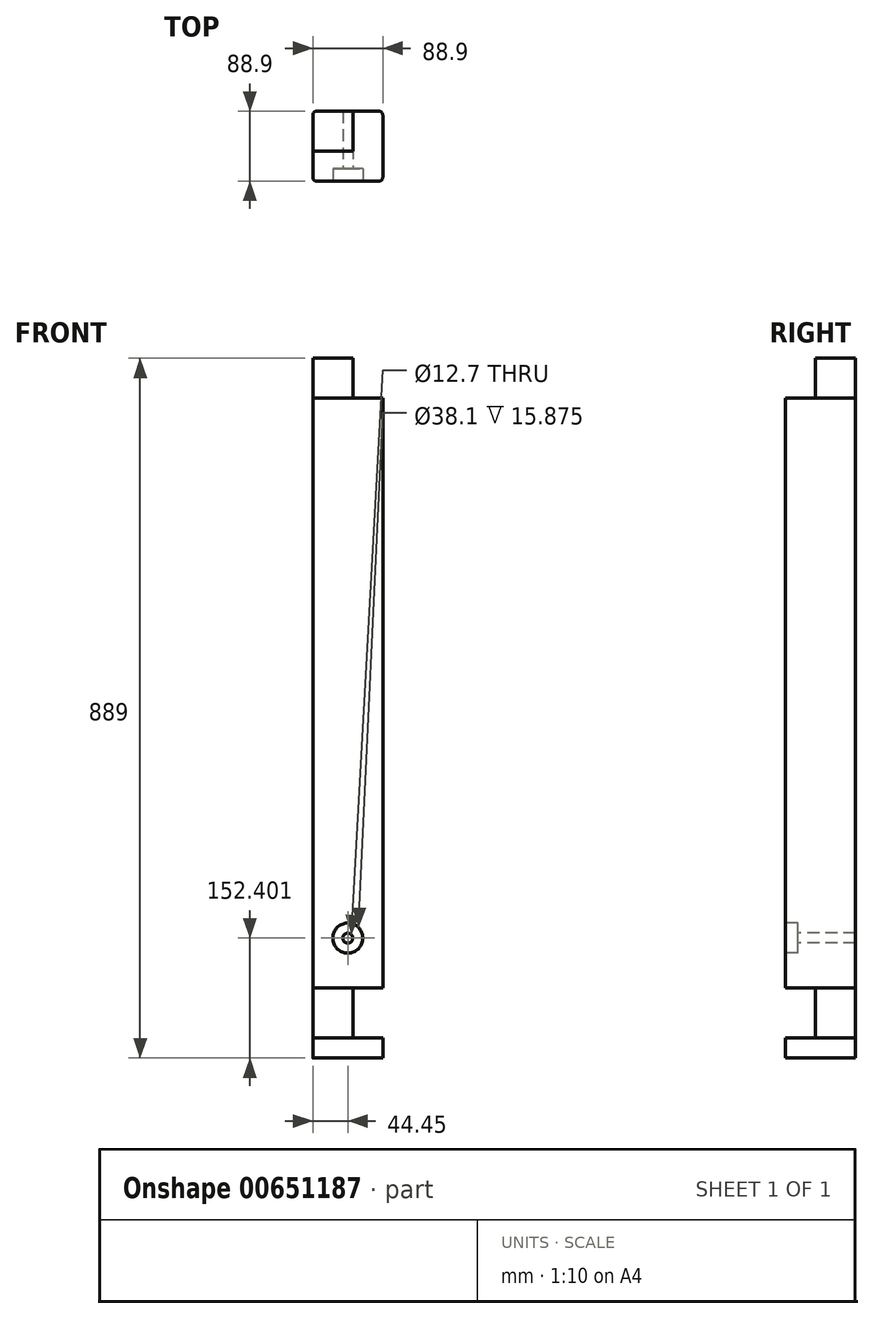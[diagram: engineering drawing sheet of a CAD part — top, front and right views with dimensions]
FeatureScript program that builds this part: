
annotation { "Feature Type Name" : "Feature", "Feature Type Description" : "" }
export const myFeature = defineFeature(function(context is Context, id is Id, definition is map)
    precondition{}
    {
        {
            var Q0;
            Q0=qCreatedBy(makeId("Right.planeOp"),FACE);
            var sketch = newSketch(context, id + "F0", { "sketchPlane" : qUnion([Q0])});
            skLineSegment(sketch, "E0", {"start": v(26.36, 525) * mm, "end": v(26.36, -364) * mm});
            skLineSegment(sketch, "E1", {"start": v(26.36, -364) * mm, "end": v(-62.54, -364) * mm});
            skLineSegment(sketch, "E2", {"start": v(-62.54, -364) * mm, "end": v(-62.54, -338.6) * mm});
            skLineSegment(sketch, "E3", {"start": v(-62.54, -338.6) * mm, "end": v(-24.44, -338.6) * mm});
            skLineSegment(sketch, "E4", {"start": v(-24.44, -338.6) * mm, "end": v(-24.44, -275.1) * mm});
            skLineSegment(sketch, "E5", {"start": v(-24.44, -275.1) * mm, "end": v(-62.54, -275.1) * mm});
            skLineSegment(sketch, "E6", {"start": v(-62.54, -275.1) * mm, "end": v(-62.54, 474.2) * mm});
            skLineSegment(sketch, "E7", {"start": v(-62.54, 474.2) * mm, "end": v(-24.44, 474.2) * mm});
            skLineSegment(sketch, "E8", {"start": v(-24.44, 474.2) * mm, "end": v(-24.44, 525) * mm});
            skLineSegment(sketch, "E9", {"start": v(-24.44, 525) * mm, "end": v(26.36, 525) * mm});
            skSolve(sketch);
        }
        {
            var Q0;
            Q0=makeQuery(id+"F0.imprint","IMPRINT",FACE,{"disambiguationData":[TD([[makeQuery(id+"F0.imprint","IMPRINT",EDGE,{"derivedFrom":sQuery(id+"F0.wireOp",EDGE,"E0")}),-1.0]])]});
            extrude(context, id + "F1", {"entities" : qUnion([Q0]), "depth" : 88.9 * mm, "offsetDistance" : 25.4 * mm, "symmetric" : true});
        }
        {
            var Q0;
            Q0=makeQuery(id+"F1.opExtrude","CAP_EDGE",EDGE,{"disambiguationData":[OSD([sQuery(id+"F0.wireOp",EDGE,"E6")])],"isStart":false});
            var Q1;
            Q1=makeQuery(id+"F1.opExtrude","CAP_EDGE",EDGE,{"disambiguationData":[OSD([sQuery(id+"F0.wireOp",EDGE,"E2")])],"isStart":false});
            var Q2;
            Q2=makeQuery(id+"F1.opExtrude","CAP_EDGE",EDGE,{"disambiguationData":[OSD([sQuery(id+"F0.wireOp",EDGE,"E2")])],"isStart":true});
            var Q3;
            Q3=makeQuery(id+"F1.opExtrude","CAP_EDGE",EDGE,{"disambiguationData":[OSD([sQuery(id+"F0.wireOp",EDGE,"E6")])],"isStart":true});
            var Q4;
            Q4=makeQuery(id+"F1.opExtrude","CAP_EDGE",EDGE,{"disambiguationData":[OSD([sQuery(id+"F0.wireOp",EDGE,"E0")])],"isStart":false});
            var Q5;
            Q5=makeQuery(id+"F1.opExtrude","CAP_EDGE",EDGE,{"disambiguationData":[OSD([sQuery(id+"F0.wireOp",EDGE,"E0")])],"isStart":true});
            fillet(context, id + "F2", {"entities" : qUnion([Q0, Q1, Q2, Q3, Q4, Q5]), "radius" : 5.08 * mm, "tangentPropagation" : true, "allowEdgeOverflow" : false});
        }
        {
            var Q0;
            Q0=qCreatedBy(makeId("Front.planeOp"),FACE);
            var sketch = newSketch(context, id + "F3", { "sketchPlane" : qUnion([Q0])});
            skLineSegment(sketch, "E10.0", {"start": v(44.45, 525) * mm, "end": v(6.35, 525) * mm});
            skLineSegment(sketch, "E11.0", {"start": v(44.45, 474.2) * mm, "end": v(44.45, 525) * mm});
            skLineSegment(sketch, "E12.0", {"start": v(39.37, 474.2) * mm, "end": v(6.35, 474.2) * mm});
            skLineSegment(sketch, "E13.0", {"start": v(39.37, 474.2) * mm, "end": v(44.45, 474.2) * mm});
            skLineSegment(sketch, "E14", {"start": v(6.35, 525) * mm, "end": v(6.35, 474.2) * mm});
            skLineSegment(sketch, "E15.0", {"start": v(39.37, -275.1) * mm, "end": v(6.35, -275.1) * mm});
            skLineSegment(sketch, "E16.0", {"start": v(44.45, -275.1) * mm, "end": v(39.37, -275.1) * mm});
            skLineSegment(sketch, "E17.0", {"start": v(44.45, -338.6) * mm, "end": v(44.45, -275.1) * mm});
            skLineSegment(sketch, "E18.0", {"start": v(39.37, -338.6) * mm, "end": v(6.35, -338.6) * mm});
            skLineSegment(sketch, "E19.0", {"start": v(39.37, -338.6) * mm, "end": v(44.45, -338.6) * mm});
            skLineSegment(sketch, "E20", {"start": v(6.35, -275.1) * mm, "end": v(6.35, -338.6) * mm});
            skSolve(sketch);
        }
        {
            var Q0;
            Q0=qSketchRegion(id+"F3",true);
            extrude(context, id + "F4", {"entities" : qUnion([Q0]), "operationType" : NewBodyOperationType.REMOVE, "oppositeDirection" : true, "depth" : 101.6 * mm, "offsetDistance" : 25.4 * mm, "symmetric" : true});
        }
        {
            var Q0;
            Q0=qCreatedBy(makeId("Front.planeOp"),FACE);
            var sketch = newSketch(context, id + "F5", { "sketchPlane" : qUnion([Q0])});
            skCircle(sketch, "E21", {"center": v(0, -211.6) * mm, "radius": 6.35 * mm});
            skSolve(sketch);
        }
        {
            var Q0;
            Q0=qSketchRegion(id+"F5",true);
            extrude(context, id + "F6", {"entities" : qUnion([Q0]), "operationType" : NewBodyOperationType.REMOVE, "endBound" : BoundingType.THROUGH_ALL, "oppositeDirection" : true, "depth" : 25.4 * mm, "offsetDistance" : 25.4 * mm, "hasSecondDirection" : true, "secondDirectionBound" : BoundingType.THROUGH_ALL, "secondDirectionOppositeDirection" : false, "secondDirectionDepth" : 25.4 * mm});
        }
        {
            var Q0;
            Q0=makeQuery(id+"F1.opExtrude","SWEPT_FACE",FACE,{"disambiguationData":[OSD([sQuery(id+"F0.wireOp",EDGE,"E6")])]});
            var sketch = newSketch(context, id + "F7", { "sketchPlane" : qUnion([Q0])});
            skCircle(sketch, "E22", {"center": v(0, -211.6) * mm, "radius": 19.05 * mm});
            skSolve(sketch);
        }
        {
            var Q0;
            Q0=makeQuery(id+"F7.imprint","IMPRINT",FACE,{"disambiguationData":[TD([[makeQuery(id+"F7.imprint","IMPRINT",EDGE,{"derivedFrom":sQuery(id+"F7.wireOp",EDGE,"E22")}),1.0]])]});
            extrude(context, id + "F8", {"entities" : qUnion([Q0]), "operationType" : NewBodyOperationType.REMOVE, "oppositeDirection" : true, "depth" : 15.88 * mm, "offsetDistance" : 25.4 * mm});
        }
    });
